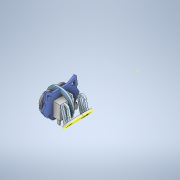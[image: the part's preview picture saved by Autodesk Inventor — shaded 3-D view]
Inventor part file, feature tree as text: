
AUTODESK INVENTOR PART (.ipt)
format: ipt  version: 2020.3 (Build 243373000, 373)  size: 4,056,064 bytes
history: native  units: mm
features: other x83, direct_edit x1, sketch x1
ambient origin geometry x8: Origin, YZ Plane, XZ Plane, XY Plane, X Axis, Y Axis, Z Axis, Center Point
bodies: Solid1 (feature_tree), Solid2 (feature_tree), Solid3 (feature_tree), Solid4 (feature_tree), Solid5 (feature_tree), Solid6 (feature_tree), Solid7 (feature_tree), Solid8 (feature_tree), Solid9 (feature_tree), Solid10 (feature_tree), Solid11 (feature_tree), Solid12 (feature_tree), Solid13 (feature_tree), Solid14 (feature_tree), Solid15 (feature_tree), Solid16 (feature_tree), Solid17 (feature_tree), Solid18 (feature_tree), Solid19 (feature_tree), Solid20 (feature_tree), Solid21 (feature_tree), Solid22 (feature_tree), Solid23 (feature_tree), Solid24 (feature_tree), Solid25 (feature_tree), Solid26 (feature_tree), Solid27 (feature_tree), Solid28 (feature_tree), Solid29 (feature_tree), Solid30 (feature_tree), Solid31 (feature_tree), Solid32 (feature_tree), Solid33 (feature_tree), Solid34 (feature_tree), Solid35 (feature_tree), Solid36 (feature_tree), Solid37 (feature_tree), Solid38 (feature_tree), Solid39 (feature_tree), Solid40 (feature_tree), Solid41 (feature_tree), Solid42 (feature_tree), Solid43 (feature_tree), Solid44 (feature_tree), Solid45 (feature_tree), Solid46 (feature_tree), Solid47 (feature_tree), Solid48 (feature_tree), Solid49 (feature_tree), Solid50 (feature_tree), Solid51 (feature_tree), Solid52 (feature_tree), Solid53 (feature_tree), Solid54 (feature_tree), Solid55 (feature_tree), Solid56 (feature_tree), Solid57 (feature_tree), Solid58 (feature_tree), Solid59 (feature_tree), Solid60 (feature_tree), Solid61 (feature_tree), Solid62 (feature_tree), Solid63 (feature_tree), Solid64 (feature_tree), Solid65 (feature_tree), Solid66 (feature_tree), Solid67 (feature_tree), Solid68 (feature_tree), Solid69 (feature_tree), Solid70 (feature_tree), Solid71 (feature_tree), Solid72 (feature_tree), Solid73 (feature_tree), Solid74 (feature_tree), Solid75 (feature_tree), Solid76 (feature_tree), Solid77 (feature_tree), Solid78 (feature_tree), Solid79 (feature_tree), Solid80 (feature_tree), Solid81 (feature_tree)
feature tree (85):
  other  "head _1_.iam"
  other  "Brophy HC-SR04-UltrasonicSensor _1_.iam:1::HC-SR04-UltrasonicSensor v7.ipt:1"
  other  "Brophy HC-SR04-UltrasonicSensor _1_.iam:1::HC-SR04-UltrasonicSensor v7_1.ipt:1"
  other  "Brophy HC-SR04-UltrasonicSensor _1_.iam:1::HC-SR04-UltrasonicSensor v7_2.ipt:1"
  other  "Brophy HC-SR04-UltrasonicSensor _1_.iam:1::HC-SR04-UltrasonicSensor v7_3.ipt:1"
  other  "Brophy HC-SR04-UltrasonicSensor _1_.iam:1::HC-SR04-UltrasonicSensor v7_4.ipt:1"
  other  "Brophy HC-SR04-UltrasonicSensor _1_.iam:1::HC-SR04-UltrasonicSensor v7_5.ipt:1"
  other  "Brophy HC-SR04-UltrasonicSensor _1_.iam:1::HC-SR04-UltrasonicSensor v7_6.ipt:1"
  other  "Brophy HC-SR04-UltrasonicSensor _1_.iam:1::HC-SR04-UltrasonicSensor v7_7.ipt:1"
  other  "Brophy HC-SR04-UltrasonicSensor _1_.iam:1::HC-SR04-UltrasonicSensor v7_8.ipt:1"
  other  "Brophy HC-SR04-UltrasonicSensor _1_.iam:1::HC-SR04-UltrasonicSensor v7_9.ipt:1"
  other  "Brophy HC-SR04-UltrasonicSensor _1_.iam:1::Part 72.ipt:1"
  other  "Brophy HC-SR04-UltrasonicSensor _1_.iam:1::HC-SR04-UltrasonicSensor v7_10.ipt:1"
  other  "Brophy HC-SR04-UltrasonicSensor _1_.iam:1::HC-SR04-UltrasonicSensor v7_11.ipt:1"
  other  "Brophy HC-SR04-UltrasonicSensor _1_.iam:1::Part 70.ipt:1"
  other  "Brophy HC-SR04-UltrasonicSensor _1_.iam:1::HC-SR04-UltrasonicSensor v7_12.ipt:1"
  other  "Brophy HC-SR04-UltrasonicSensor _1_.iam:1::HC-SR04-UltrasonicSensor v7_13.ipt:1"
  other  "Brophy HC-SR04-UltrasonicSensor _1_.iam:1::HC-SR04-UltrasonicSensor v7_14.ipt:1"
  other  "Brophy HC-SR04-UltrasonicSensor _1_.iam:1::HC-SR04-UltrasonicSensor v7_15.ipt:1"
  other  "Brophy HC-SR04-UltrasonicSensor _1_.iam:1::HC-SR04-UltrasonicSensor v7_16.ipt:1"
  other  "Brophy HC-SR04-UltrasonicSensor _1_.iam:1::HC-SR04-UltrasonicSensor v7_17.ipt:1"
  other  "Brophy HC-SR04-UltrasonicSensor _1_.iam:1::HC-SR04-UltrasonicSensor v7_18.ipt:1"
  other  "Brophy HC-SR04-UltrasonicSensor _1_.iam:1::HC-SR04-UltrasonicSensor v7_19.ipt:1"
  other  "Brophy HC-SR04-UltrasonicSensor _1_.iam:1::Part 68.ipt:1"
  other  "Brophy HC-SR04-UltrasonicSensor _1_.iam:1::HC-SR04-UltrasonicSensor v7_20.ipt:1"
  other  "Brophy HC-SR04-UltrasonicSensor _1_.iam:1::HC-SR04-UltrasonicSensor v7_21.ipt:1"
  other  "Brophy HC-SR04-UltrasonicSensor _1_.iam:1::HC-SR04-UltrasonicSensor v7_22.ipt:1"
  other  "Brophy HC-SR04-UltrasonicSensor _1_.iam:1::HC-SR04-UltrasonicSensor v7_23.ipt:1"
  other  "Brophy HC-SR04-UltrasonicSensor _1_.iam:1::Part 62.ipt:1"
  other  "Brophy HC-SR04-UltrasonicSensor _1_.iam:1::HC-SR04-UltrasonicSensor v7_24.ipt:1"
  other  "Brophy HC-SR04-UltrasonicSensor _1_.iam:1::HC-SR04-UltrasonicSensor v7_25.ipt:1"
  other  "Brophy HC-SR04-UltrasonicSensor _1_.iam:1::HC-SR04-UltrasonicSensor v7_26.ipt:1"
  other  "Brophy HC-SR04-UltrasonicSensor _1_.iam:1::Part 58.ipt:1"
  other  "Brophy HC-SR04-UltrasonicSensor _1_.iam:1::Part 63.ipt:1"
  other  "Brophy HC-SR04-UltrasonicSensor _1_.iam:1::HC-SR04-UltrasonicSensor v7_27.ipt:1"
  other  "Brophy HC-SR04-UltrasonicSensor _1_.iam:1::HC-SR04-UltrasonicSensor v7_28.ipt:1"
  other  "Brophy HC-SR04-UltrasonicSensor _1_.iam:1::Part 69.ipt:1"
  other  "Brophy HC-SR04-UltrasonicSensor _1_.iam:1::Part 67.ipt:1"
  other  "Brophy HC-SR04-UltrasonicSensor _1_.iam:1::HC-SR04-UltrasonicSensor v7_29.ipt:1"
  other  "Brophy HC-SR04-UltrasonicSensor _1_.iam:1::Part 64.ipt:1"
  other  "Brophy HC-SR04-UltrasonicSensor _1_.iam:1::HC-SR04-UltrasonicSensor v7_30.ipt:1"
  other  "Brophy HC-SR04-UltrasonicSensor _1_.iam:1::HC-SR04-UltrasonicSensor v7_31.ipt:1"
  other  "Brophy HC-SR04-UltrasonicSensor _1_.iam:1::Part 65.ipt:1"
  other  "Brophy HC-SR04-UltrasonicSensor _1_.iam:1::HC-SR04-UltrasonicSensor v7_32.ipt:1"
  other  "Brophy HC-SR04-UltrasonicSensor _1_.iam:1::HC-SR04-UltrasonicSensor v7_33.ipt:1"
  other  "Brophy HC-SR04-UltrasonicSensor _1_.iam:1::Part 61.ipt:1"
  other  "Brophy HC-SR04-UltrasonicSensor _1_.iam:1::HC-SR04-UltrasonicSensor v7_34.ipt:1"
  other  "Brophy HC-SR04-UltrasonicSensor _1_.iam:1::HC-SR04-UltrasonicSensor v7_35.ipt:1"
  other  "Brophy HC-SR04-UltrasonicSensor _1_.iam:1::HC-SR04-UltrasonicSensor v7_36.ipt:1"
  other  "Brophy HC-SR04-UltrasonicSensor _1_.iam:1::HC-SR04-UltrasonicSensor v7_37.ipt:1"
  other  "Brophy HC-SR04-UltrasonicSensor _1_.iam:1::HC-SR04-UltrasonicSensor v7_38.ipt:1"
  other  "Brophy HC-SR04-UltrasonicSensor _1_.iam:1::HC-SR04-UltrasonicSensor v7_39.ipt:1"
  other  "Brophy HC-SR04-UltrasonicSensor _1_.iam:1::HC-SR04-UltrasonicSensor v7_40.ipt:1"
  other  "Brophy HC-SR04-UltrasonicSensor _1_.iam:1::HC-SR04-UltrasonicSensor v7_41.ipt:1"
  other  "Brophy HC-SR04-UltrasonicSensor _1_.iam:1::HC-SR04-UltrasonicSensor v7_42.ipt:1"
  other  "Brophy HC-SR04-UltrasonicSensor _1_.iam:1::Part 71.ipt:1"
  other  "Brophy HC-SR04-UltrasonicSensor _1_.iam:1::HC-SR04-UltrasonicSensor v7_43.ipt:1"
  other  "Brophy HC-SR04-UltrasonicSensor _1_.iam:1::HC-SR04-UltrasonicSensor v7_44.ipt:1"
  other  "Brophy HC-SR04-UltrasonicSensor _1_.iam:1::Part 66.ipt:1"
  other  "Brophy HC-SR04-UltrasonicSensor _1_.iam:1::HC-SR04-UltrasonicSensor v7_45.ipt:1"
  other  "Brophy HC-SR04-UltrasonicSensor _1_.iam:1::HC-SR04-UltrasonicSensor v7_46.ipt:1"
  other  "Brophy HC-SR04-UltrasonicSensor _1_.iam:1::HC-SR04-UltrasonicSensor v7_47.ipt:1"
  other  "Brophy HC-SR04-UltrasonicSensor _1_.iam:1::Part 59.ipt:1"
  other  "Brophy HC-SR04-UltrasonicSensor _1_.iam:1::HC-SR04-UltrasonicSensor v7_48.ipt:1"
  other  "Brophy HC-SR04-UltrasonicSensor _1_.iam:1::Part 60.ipt:1"
  other  "Brophy HC-SR04-UltrasonicSensor _1_.iam:1::HC-SR04-UltrasonicSensor v7_49.ipt:1"
  other  "Brophy HC-SR04-UltrasonicSensor _1_.iam:1::HC-SR04-UltrasonicSensor v7_50.ipt:1"
  other  "Brophy HC-SR04-UltrasonicSensor _1_.iam:1::HC-SR04-UltrasonicSensor v7_51.ipt:1"
  other  "Brophy HC-SR04-UltrasonicSensor _1_.iam:1::HC-SR04-UltrasonicSensor v7_52.ipt:1"
  other  "Brophy HC-SR04-UltrasonicSensor _1_.iam:1::HC-SR04-UltrasonicSensor v7_53.ipt:1"
  other  "Brophy HC-SR04-UltrasonicSensor _1_.iam:1::HC-SR04-UltrasonicSensor v7_54.ipt:1"
  other  "Brophy HC-SR04-UltrasonicSensor _1_.iam:1::HC-SR04-UltrasonicSensor v7_55.ipt:1"
  other  "Brophy HC-SR04-UltrasonicSensor _1_.iam:1::HC-SR04-UltrasonicSensor v7_56.ipt:1"
  other  "Part 12.ipt:1"
  other  "Part 1.ipt:1"
  other  "Part 1_1.ipt:1"
  other  "Part 5.ipt:1"
  other  "Part 3.ipt:1"
  other  "Part 13.ipt:1"
  other  "Part 4.ipt:1"
  other  "Part 2.ipt:1"
  other  "Part 13.ipt:2"
  direct_edit  "Direct Edit1"
  sketch  "Sketch1"  dims[d0=20.0mm d1=4.0mm]
  other  "Size1"
